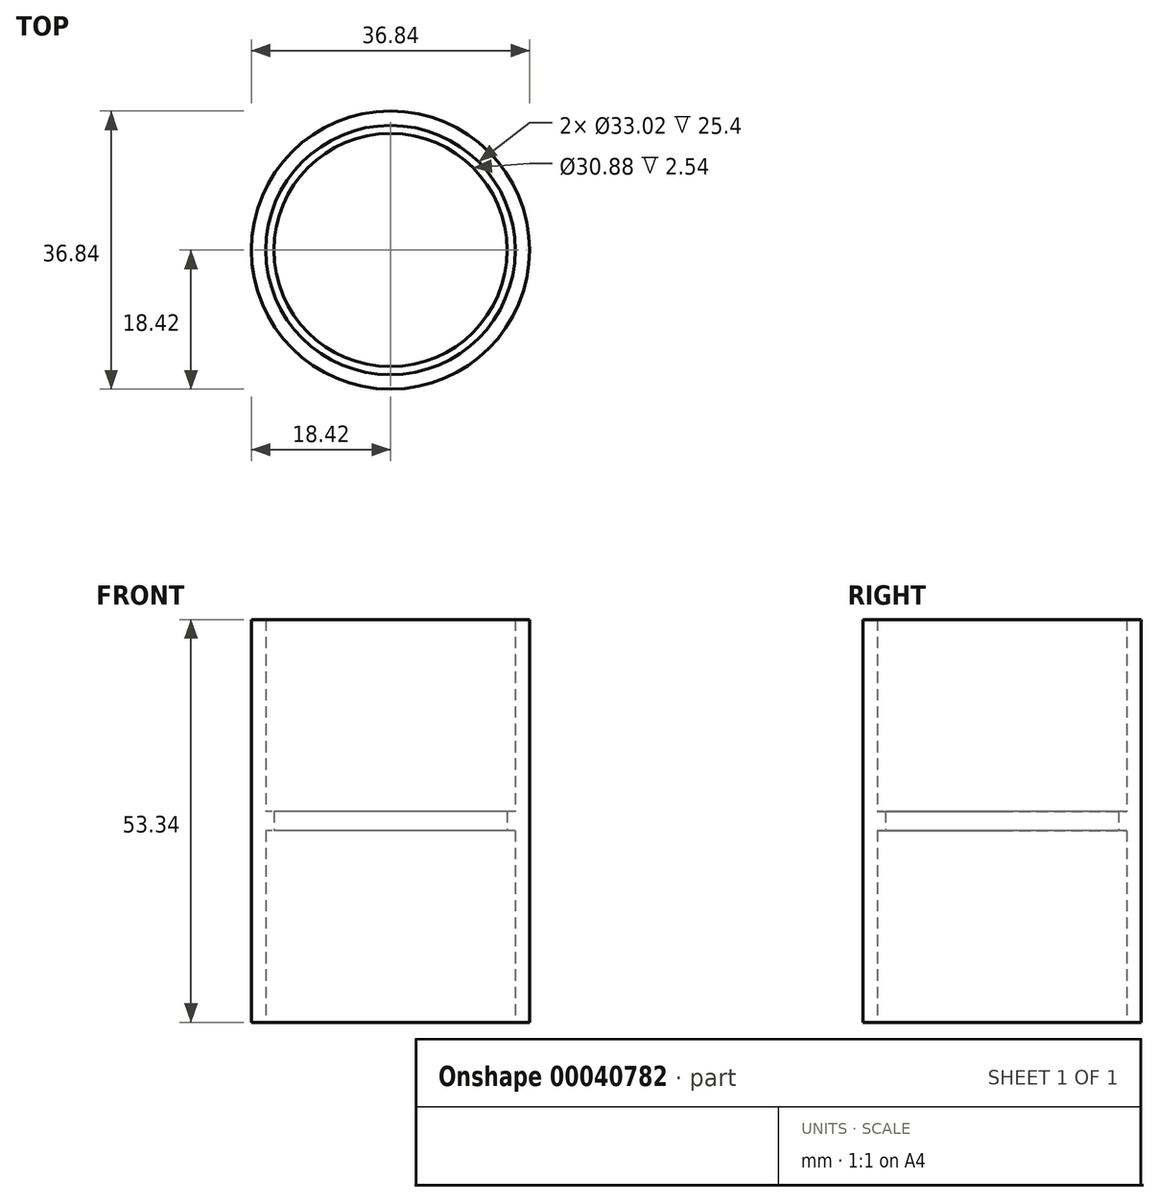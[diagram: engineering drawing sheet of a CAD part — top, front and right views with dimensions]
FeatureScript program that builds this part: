
annotation { "Feature Type Name" : "Feature", "Feature Type Description" : "" }
export const myFeature = defineFeature(function(context is Context, id is Id, definition is map)
    precondition{}
    {
        {
            var Q0;
            Q0=qCreatedBy(makeId("Top.planeOp"),FACE);
            var sketch = newSketch(context, id + "F0", { "sketchPlane" : qUnion([Q0])});
            skCircle(sketch, "E0", {"center": v(0, 0) * mm, "radius": 18.41 * mm});
            skCircle(sketch, "E1", {"center": v(0, 0) * mm, "radius": 16.51 * mm});
            skSolve(sketch);
        }
        {
            var Q0;
            Q0=makeQuery(id+"F0.imprint","IMPRINT",FACE,{"disambiguationData":[TD([[makeQuery(id+"F0.imprint","IMPRINT",EDGE,{"derivedFrom":sQuery(id+"F0.wireOp",EDGE,"E0")}),1.0]])]});
            extrude(context, id + "F1", {"entities" : qUnion([Q0]), "depth" : 25.4 * mm});
        }
        {
            var Q0;
            Q0=makeQuery(id+"F1.opExtrude","CAP_FACE",FACE,{"disambiguationData":[OSD([sQuery(id+"F0.wireOp",EDGE,"E0"),sQuery(id+"F0.wireOp",EDGE,"E1")])],"isStart":false});
            cPlane(context, id + "F2", {"entities" : qUnion([Q0]), "cplaneType" : CPlaneType.OFFSET, "offset" : 0 * mm, "oppositeDirection" : true, "width" : 152.4 * mm, "height" : 152.4 * mm});
        }
        {
            var Q0;
            Q0=qCreatedBy(id+"F2.planeOp",FACE);
            var sketch = newSketch(context, id + "F3", { "sketchPlane" : qUnion([Q0])});
            skCircle(sketch, "E2.0", {"center": v(0, 0) * mm, "radius": 16.51 * mm});
            skCircle(sketch, "E3", {"center": v(0, 0) * mm, "radius": 15.44 * mm});
            skCircle(sketch, "E4.0", {"center": v(0, 0) * mm, "radius": 18.41 * mm});
            skSolve(sketch);
        }
        {
            var Q0;
            Q0=makeQuery(id+"F3.imprint","IMPRINT",FACE,{"disambiguationData":[TD([[makeQuery(id+"F3.imprint","IMPRINT",EDGE,{"derivedFrom":sQuery(id+"F3.wireOp",EDGE,"E2.0")}),1.0]])]});
            var Q1;
            Q1=makeQuery(id+"F3.imprint","IMPRINT",FACE,{"disambiguationData":[TD([[makeQuery(id+"F3.imprint","IMPRINT",EDGE,{"derivedFrom":sQuery(id+"F3.wireOp",EDGE,"E2.0")}),-1.0]])]});
            extrude(context, id + "F4", {"entities" : qUnion([Q0, Q1]), "operationType" : NewBodyOperationType.ADD, "depth" : 2.54 * mm});
        }
        {
            var Q0;
            Q0=makeQuery(id+"F4.opExtrude","CAP_FACE",FACE,{"disambiguationData":[OSD([sQuery(id+"F3.wireOp",EDGE,"E3"),sQuery(id+"F3.wireOp",EDGE,"E4.0")])],"isStart":false});
            var sketch = newSketch(context, id + "F5", { "sketchPlane" : qUnion([Q0])});
            skCircle(sketch, "E5.0", {"center": v(0, 0) * mm, "radius": 15.44 * mm});
            skCircle(sketch, "E6.0", {"center": v(0, 0) * mm, "radius": 18.41 * mm});
            skCircle(sketch, "E7", {"center": v(0, 0) * mm, "radius": 16.51 * mm});
            skSolve(sketch);
        }
        {
            var Q0;
            Q0=makeQuery(id+"F5.imprint","IMPRINT",FACE,{"disambiguationData":[TD([[makeQuery(id+"F5.imprint","IMPRINT",EDGE,{"derivedFrom":sQuery(id+"F5.wireOp",EDGE,"E6.0")}),1.0]])]});
            extrude(context, id + "F6", {"entities" : qUnion([Q0]), "operationType" : NewBodyOperationType.ADD, "depth" : 25.4 * mm});
        }
    });
